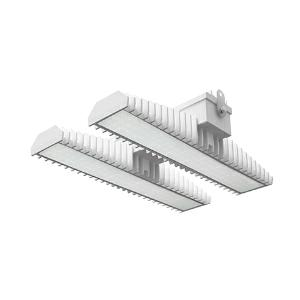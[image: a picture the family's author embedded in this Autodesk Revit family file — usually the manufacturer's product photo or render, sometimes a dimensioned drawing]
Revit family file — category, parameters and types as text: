
# Revit family: 3f_filippi_-_3f_lem_ampio_3f_filippi_-_58900_a0812_-_3f_lem_2_led_100_dali_cr_ampio___vs_98ae
name_source: partatom
category: Lighting Fixtures
units: mm (PartAtom-declared; Revit-internal decimal feet)

## family parameters
Cut with Voids When Loaded = No
Host = Face
Light Source = No
Part Type = Normal
Room Calculation Point = No
Round Connector Dimension = Use Diameter
Shared = No

## types (1)
- 3F Filippi - 3F LEM Ampio (1 x LED, 13304 lm, 109 W, 4000 K)
    Apparent Load = 109 VA
    Approval mark = CE
    CIE Flux Codes = 67 90 97 100 100
    Color Rendering = 80
    Color Temperature = 4000 K
    Control Gear = Electronic transformer
    Default Elevation = 1800 mm
    Description = Industrial luminaire with high light output and high luminous efficiency designed with the most innovative technologies for environments with temperature up to 55°C.

ILLUMINOTECHNICAL
Luminous efficiency 100% (DLOR 98%, ULOR 2%).
Initial luminous flux of the luminaire 13304 lm.
Direct symmetric wide distribution: the illuminated area has a rectangular shape.
Installation Interdistance Transv.D = 1.24 x hu - Long.D = 1.20 x hu.
Tabular UGR (CIE 117 - 4H-8H; S=0.25H; 70/50/20): RUG 22.1 - 22.2.
Beam angle: 82° - 83°.
Luminous efficacy 122 lm/W.
Lifetime (L93/B10): 30000 h. (tq+25°C)
Lifetime (L90/B10): 50000 h. (tq+25°C)
Lifetime (L85/B10): 80000 h. (tq+25°C)
Lifetime (L80/B10): 100000 h. (tq+25°C)
Lifetime (L85/B10): 50000 h. (tq+55°C)
Sudden decreased luminous flux after 50000 hours: 0% (C0).
Photobiological safety in compliance with IEC/TR 62778: RG0 risk exempt, (IEC 62471).
In compliance with IEC/EN 62722-2-1 - IEC/EN 62717 standards.

SOURCE
2 Mid-Power linear LED modules 50W/840.
Energy efficiency class (UE 2019/2020 - UE 2019/2015): C.
CIE 13.3 Colour rendering index: CRI >80 (R9 <50%).
IES TM-30 Fidelity Index: Rf = 84 Rg = 95.
CCT nominal colour temperature 4000 K.
Colour initial tolerance (MacAdam): SDCM 3.

MECHANICAL
Passive modular heatsinks in die-casted aluminium, painted in white colour.
To optimize the thermal management of the LED module, the heatsinks are oversized and provided with self-cleaning of cooling fins.
Wiring body in aluminium and galvanised steel anchored solidly to the sinks and thermally separated.
3F Lens lenses with high luminous efficiency, transparent methacrylate (PMMA), fixed to the LED modules.
Fixing brackets in stainless steel.
Luminaire with limited surface temperature. - D - (EN 60598-2-24)
Dimensions: 470x542 mm, height 133 mm. Weight 10.18 kg.
IP65 protection degree.
Mechanical strength to impacts IK06 (1 joule).
Glow-wire test resistance 650°C.

ELECTRICAL
Halogen Free DALI-2 DATI (Parts 251, 252, 253), PUSH-DIM, electronic wiring 230V-50/60Hz, power factor 0.97 at full load, THD <25%, constant output current, class I, 1 driver, 1 DALI addresse.
Power of the luminaire 109 W.
ENEC - CE.
Flicker: <4%.
Luminaire compliant with EN 60598-2-22 for power supply from a centralised emergency system CPSS (Central Power Supply System), not incorporated in the luminaire - high risk areas excluded. The default power and flux are 100% in AC and 15% in DC.
Ambient temperature from -30°C to +55°C.
Temperature class T6 max 85°C.
Quick connection via M25 5P connector with 9-13 mm tightening range.
Power unit positioned on a separate compartment by the LED module to ensure optimum temperatures of cabling components, to be inspectable and maintainable.
Relative humidity UR: <85%.

INSTALLATION
Ceiling / Suspended / Wall.
All accessories dedicated to this product are available on the Catalog and on our website www.3F-Filippi.com.

ACCESSORIES
A0812 - Anti-glare microprismatic VS moulded glass, tempered, not flammable, with sealing gasket.
One required for each light module. The pack contains 10 pieces.

APPLICATIONS
In commercial environments, exhibition and industrial areas, stores, open areas.
Applications with high ambient temperature up to 55°C.
Environments in which it is necessary a total protection against falling fragments (eg environments with foodstuffs or machines with moving parts or with extreme temperature changes), use luminaires with polycarbonate lenses.

LIGHT MANAGEMENT
Recommended minimum setting: 10%.
The luminaire, equipped with (DALI-2 DATI) driver, can be controlled manually with 3F Easy Dim technology or automatically/manually with wired or wireless DALI/D2D control systems.
The D2D driver guarantees interoperability with other devices with the same certification by making the following information available:
Device Data (Part 251), Energy Report (Part 252), Diagnosis & Maintenance (Part 253).
In electrical systems without a regulation system (manual or automatic) and DALI bus, a suitable jumper must be made on the DA-DA terminals of the appliance.

WARNING
Fixture not suitable for cold stores with an ambient temperature <0°C and/or relative humidity >85%.
Luminaire designed for disposal/recycling at end-of-life.
Replaceable (LED only) light source by a professional. Replaceable control gear by a professional.
    Height = 133 mm  [stored 0.436352 ft]
    Lamp = 1 x LED
    Lamp Light Flux = 13304 lm
    Lamp Power = 109 W
    Lamp count = 1
    Length = 470 mm
    Lifetime = 50000 h
    Luminous efficacy = 122 lm/W
    Manufacturer = 3F Filippi
    ModVariant = No
    Model = 3F Filippi - 58900+A0812 - 3F LEM 2 LED 100 DALI CR AMPIO + VS
    Mounting Place = Ceiling
    Mounting Type = Pendant
    Number of Poles = 1
    OnlyDefault = Yes
    Power Factor = 1
    Product Name = 3F Filippi - 3F LEM Ampio
    Product group = pendant luminaire
    ProductGroupID = 9
    Protection Class = Protection class I
    Protection Degree = IP 65
    RLX_Detail_Level = 1
    RLX_Emergency_Light_Flux = 0 lm
    RLX_Emergency_Type = 0
    RLX_Emergency_Type_DB = No
    RlxData = <blob elided: 97353 chars, md5=75a41922>
    Socket = socket
    Standby Power = 0 W
    System Light Flux = 13304 lm
    System Power = 109 W
    Type Comments = Product without accessories
    Type Image = 3f_filippi_-_lem_2__a0812.jpg
    URL = http://relux.com
    VarID = ---
    Voltage = 0 V
    Weight = 0.00 kg
    Width = 542 mm

note: [stored X ft] marks values corroborated as IEEE doubles in the binary element streams (Revit-internal decimal feet)

## geometry (parser evidence)
native form markers: Blend x4, Sweep x14
no freeform markers — native parametric forms only
